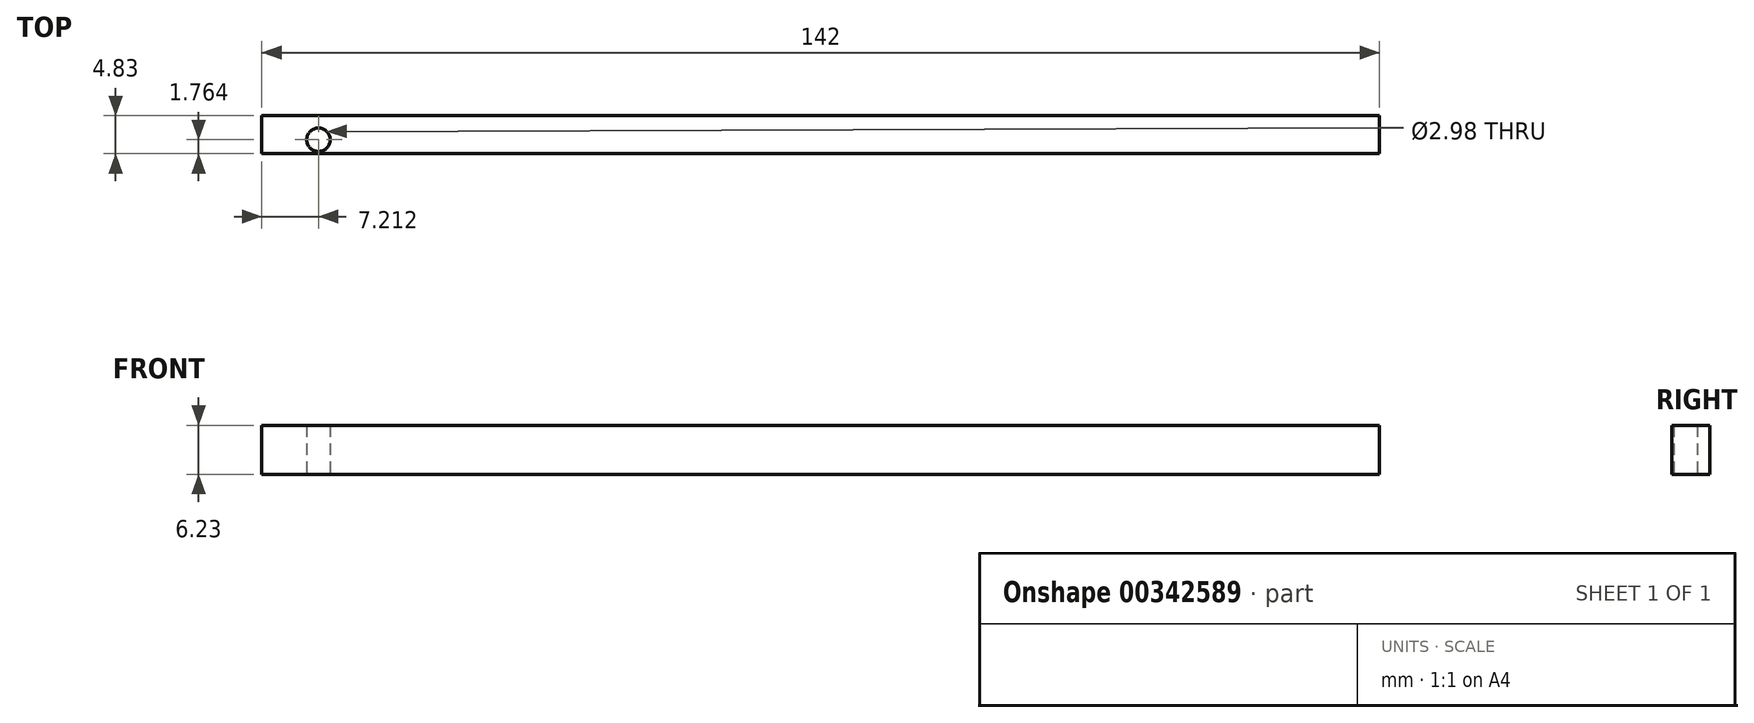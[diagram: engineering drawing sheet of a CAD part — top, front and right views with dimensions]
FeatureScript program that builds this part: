
annotation { "Feature Type Name" : "Feature", "Feature Type Description" : "" }
export const myFeature = defineFeature(function(context is Context, id is Id, definition is map)
    precondition{}
    {
        {
            var Q0;
            Q0=qCreatedBy(makeId("Front.planeOp"),FACE);
            var sketch = newSketch(context, id + "F0", { "sketchPlane" : qUnion([Q0])});
            skLineSegment(sketch, "E0.bottom", {"start": v(-70.27, 22.89) * mm, "end": v(71.73, 22.89) * mm});
            skLineSegment(sketch, "E0.top", {"start": v(-70.27, 29.12) * mm, "end": v(71.73, 29.12) * mm});
            skLineSegment(sketch, "E0.left", {"start": v(-70.27, 22.89) * mm, "end": v(-70.27, 29.12) * mm});
            skLineSegment(sketch, "E0.right", {"start": v(71.73, 22.89) * mm, "end": v(71.73, 29.12) * mm});
            skSolve(sketch);
        }
        {
            var Q0;
            Q0=makeQuery(id+"F0.imprint","IMPRINT",FACE,{"disambiguationData":[TD([[makeQuery(id+"F0.imprint","IMPRINT",EDGE,{"derivedFrom":sQuery(id+"F0.wireOp",EDGE,"E0.bottom")}),1.0]])]});
            extrude(context, id + "F1", {"entities" : qUnion([Q0]), "depth" : 4.83 * mm});
        }
        {
            var Q0;
            Q0=qCreatedBy(makeId("Top.planeOp"),FACE);
            var sketch = newSketch(context, id + "F2", { "sketchPlane" : qUnion([Q0])});
            skCircle(sketch, "E1", {"center": v(-63.06, -3.07) * mm, "radius": 1.49 * mm});
            skPoint(sketch, "E1.first.point", {"position": v(-64.54, -3.23) * mm});
            skPoint(sketch, "E1.second.point", {"position": v(-62.19, -1.86) * mm});
            skPoint(sketch, "E1.third.point", {"position": v(-63.56, -1.66) * mm});
            skSolve(sketch);
        }
        {
            var Q0;
            Q0 = qSketchRegion(id + "F2", true);
            extrude(context, id + "F3", {"entities" : qUnion([Q0]), "operationType" : NewBodyOperationType.REMOVE, "endBound" : BoundingType.THROUGH_ALL, "depth" : 25.4 * mm});
        }
    });
